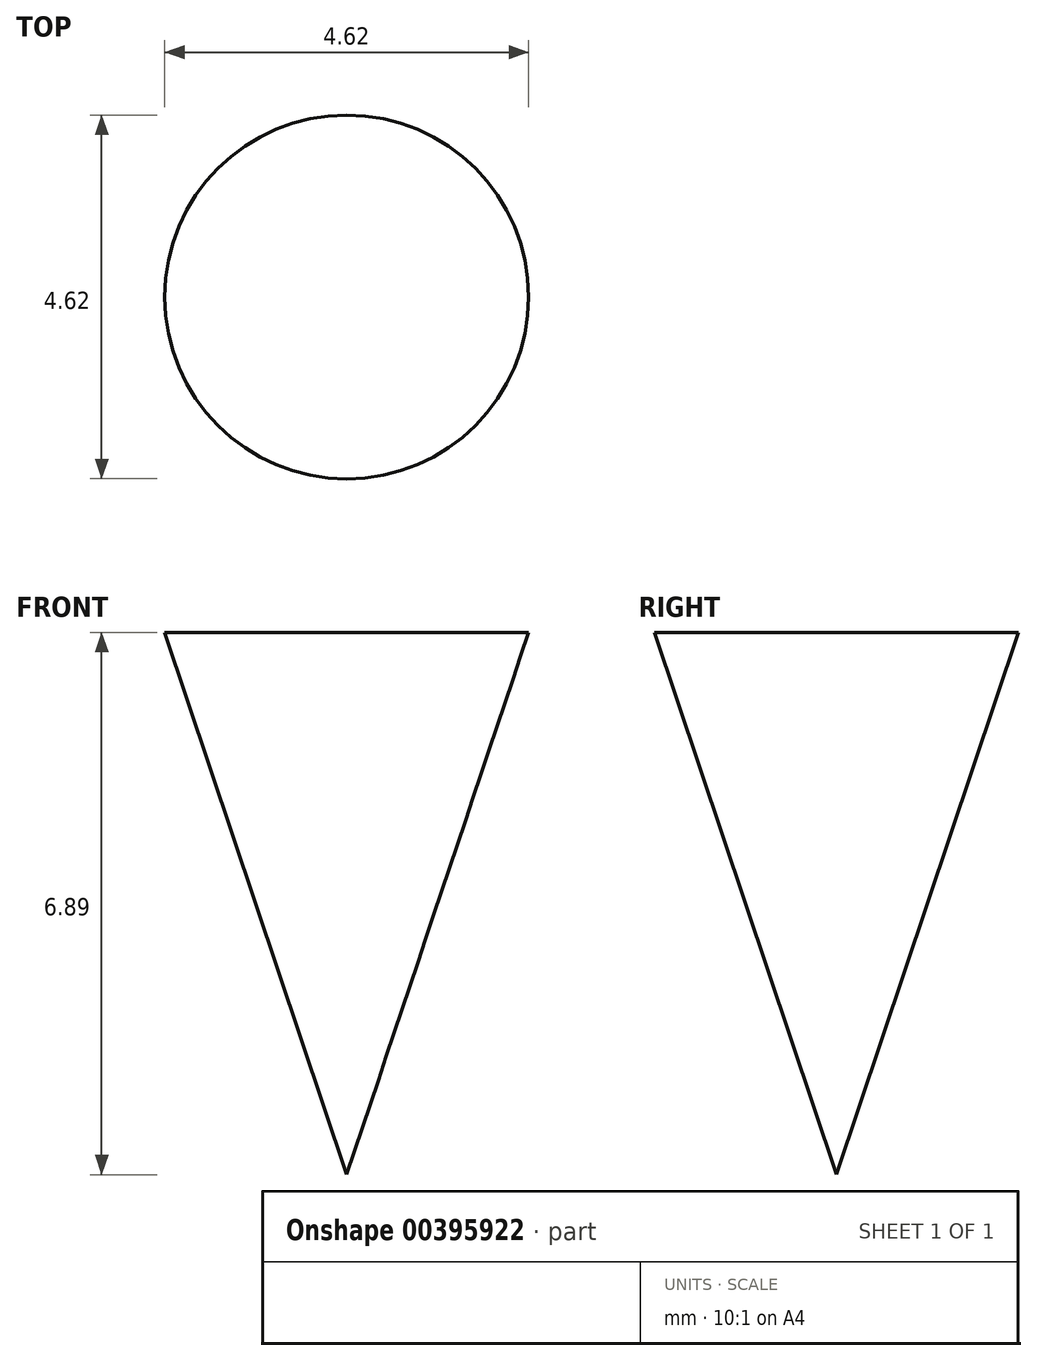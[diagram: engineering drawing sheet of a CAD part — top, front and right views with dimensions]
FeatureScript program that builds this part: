
annotation { "Feature Type Name" : "Feature", "Feature Type Description" : "" }
export const myFeature = defineFeature(function(context is Context, id is Id, definition is map)
    precondition{}
    {
        {
            var Q0;
            Q0=qCreatedBy(makeId("Front.planeOp"),FACE);
            var sketch = newSketch(context, id + "F0", { "sketchPlane" : qUnion([Q0])});
            skLineSegment(sketch, "E0", {"start": v(0, -6.89) * mm, "end": v(-2.31, 0) * mm});
            skLineSegment(sketch, "E1", {"start": v(-2.31, 0) * mm, "end": v(0, 0) * mm});
            skLineSegment(sketch, "E2", {"start": v(0, 0) * mm, "end": v(0, -6.89) * mm});
            skSolve(sketch);
        }
        {
            var Q0;
            Q0 = qSketchRegion(id + "F0", true);
            var Q1;
            Q1=sQuery(id+"F0.wireOp",EDGE,"E2");
            revolve(context, id + "F1", {"entities" : qUnion([Q0]), "axis" : qUnion([Q1]), "revolveType" : RevolveType.FULL});
        }
    });
